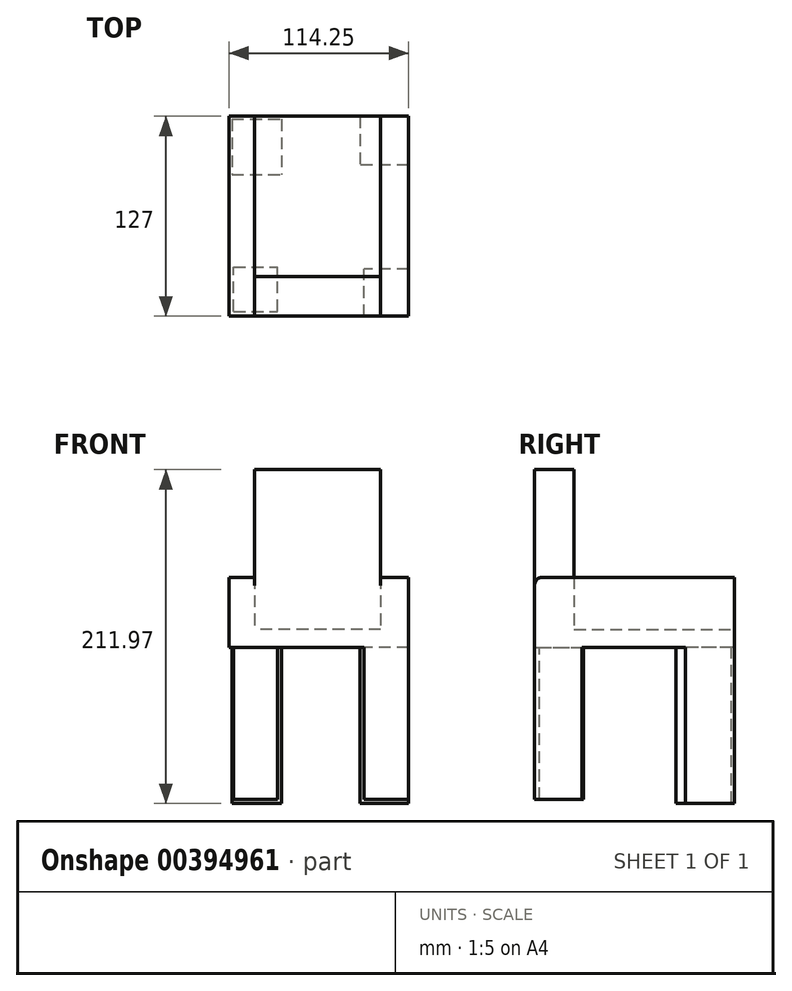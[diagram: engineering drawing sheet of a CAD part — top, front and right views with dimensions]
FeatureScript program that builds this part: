
annotation { "Feature Type Name" : "Feature", "Feature Type Description" : "" }
export const myFeature = defineFeature(function(context is Context, id is Id, definition is map)
    precondition{}
    {
        {
            var Q0;
            Q0=qCreatedBy(makeId("Front.planeOp"),FACE);
            var sketch = newSketch(context, id + "F0", { "sketchPlane" : qUnion([Q0])});
            skLineSegment(sketch, "E0.bottom", {"start": v(-64.3, 40.12) * mm, "end": v(49.96, 40.12) * mm});
            skLineSegment(sketch, "E0.top", {"start": v(-64.3, -37.67) * mm, "end": v(49.96, -37.67) * mm});
            skLineSegment(sketch, "E0.left", {"start": v(-64.3, 40.12) * mm, "end": v(-64.3, -37.67) * mm});
            skLineSegment(sketch, "E0.right", {"start": v(49.96, 40.12) * mm, "end": v(49.96, -37.67) * mm});
            skLineSegment(sketch, "E1.bottom", {"start": v(41.06, 40.12) * mm, "end": v(52.67, 40.12) * mm});
            skLineSegment(sketch, "E1.top", {"start": v(41.06, 40.12) * mm, "end": v(52.67, 40.12) * mm});
            skLineSegment(sketch, "E1.left", {"start": v(41.06, 40.12) * mm, "end": v(41.06, 40.12) * mm});
            skLineSegment(sketch, "E1.right", {"start": v(52.67, 40.12) * mm, "end": v(52.67, 40.12) * mm});
            skSolve(sketch);
        }
        {
            var Q0;
            {var subQ1=sQuery(id+"F0.wireOp",EDGE,"E0.bottom");Q0=makeQuery(id+"F0.imprint","IMPRINT",FACE,{"disambiguationData":[TD([[makeQuery(id+"F0.imprint","IMPRINT",EDGE,{"derivedFrom":subQ1}),-1.0]])]});}
            extrude(context, id + "F1", {"entities" : qUnion([Q0]), "oppositeDirection" : true, "depth" : 127 * mm});
        }
        {
            var Q0;
            Q0=makeQuery(id+"F1.opExtrude","CAP_FACE",FACE,{"disambiguationData":[OSD([sQuery(id+"F0.wireOp",EDGE,"E0.bottom"),sQuery(id+"F0.wireOp",EDGE,"E0.top"),sQuery(id+"F0.wireOp",EDGE,"E0.left"),sQuery(id+"F0.wireOp",EDGE,"E0.right"),sQuery(id+"F0.wireOp",EDGE,"E1.top")])],"isStart":false});
            var sketch = newSketch(context, id + "F2", { "sketchPlane" : qUnion([Q0])});
            skLineSegment(sketch, "E2.bottom", {"start": v(-32.22, 40.12) * mm, "end": v(48, 40.12) * mm});
            skLineSegment(sketch, "E2.top", {"start": v(-32.22, -26.36) * mm, "end": v(48, -26.36) * mm});
            skLineSegment(sketch, "E2.left", {"start": v(-32.22, 40.12) * mm, "end": v(-32.22, -26.36) * mm});
            skLineSegment(sketch, "E2.right", {"start": v(48, 40.12) * mm, "end": v(48, -26.36) * mm});
            skSolve(sketch);
        }
        {
            var Q0;
            Q0 = qSketchRegion(id + "F2", true);
            extrude(context, id + "F3", {"entities" : qUnion([Q0]), "operationType" : NewBodyOperationType.REMOVE, "oppositeDirection" : true, "depth" : 127 * mm});
        }
        {
            var Q0;
            Q0=makeQuery(id+"F1.opExtrude","CAP_FACE",FACE,{"disambiguationData":[OSD([sQuery(id+"F0.wireOp",EDGE,"E0.bottom"),sQuery(id+"F0.wireOp",EDGE,"E0.top"),sQuery(id+"F0.wireOp",EDGE,"E0.left"),sQuery(id+"F0.wireOp",EDGE,"E0.right"),sQuery(id+"F0.wireOp",EDGE,"E1.top")])],"isStart":false});
            var sketch = newSketch(context, id + "F4", { "sketchPlane" : qUnion([Q0])});
            skLineSegment(sketch, "E3.bottom", {"start": v(-49.96, 40.12) * mm, "end": v(-32.22, 40.12) * mm});
            skLineSegment(sketch, "E3.top", {"start": v(-49.96, 6.88) * mm, "end": v(-32.22, 6.88) * mm});
            skLineSegment(sketch, "E3.left", {"start": v(-49.96, 40.12) * mm, "end": v(-49.96, 6.88) * mm});
            skLineSegment(sketch, "E3.right", {"start": v(-32.22, 40.12) * mm, "end": v(-32.22, 6.88) * mm});
            skLineSegment(sketch, "E4.bottom", {"start": v(48, 40.12) * mm, "end": v(64.3, 40.12) * mm});
            skLineSegment(sketch, "E4.top", {"start": v(48, 6.88) * mm, "end": v(64.3, 6.88) * mm});
            skLineSegment(sketch, "E4.left", {"start": v(48, 40.12) * mm, "end": v(48, 6.88) * mm});
            skLineSegment(sketch, "E4.right", {"start": v(64.3, 40.12) * mm, "end": v(64.3, 6.88) * mm});
            skSolve(sketch);
        }
        {
            var Q0;
            Q0 = qSketchRegion(id + "F4", true);
            extrude(context, id + "F5", {"entities" : qUnion([Q0]), "operationType" : NewBodyOperationType.REMOVE, "oppositeDirection" : true, "depth" : 152.4 * mm});
        }
        {
            var Q0;
            Q0=makeQuery(id+"F3.boolean.opBoolean","COPY",FACE,{"derivedFrom":makeQuery(id+"F3.opExtrude","SWEPT_FACE",FACE,{"disambiguationData":[OSD([sQuery(id+"F2.wireOp",EDGE,"E2.top")])]})});
            var sketch = newSketch(context, id + "F6", { "sketchPlane" : qUnion([Q0])});
            skLineSegment(sketch, "E5.bottom", {"start": v(-48, 0) * mm, "end": v(32.22, 0) * mm});
            skLineSegment(sketch, "E5.top", {"start": v(-48, 25) * mm, "end": v(32.22, 25) * mm});
            skLineSegment(sketch, "E5.left", {"start": v(-48, 0) * mm, "end": v(-48, 25) * mm});
            skLineSegment(sketch, "E5.right", {"start": v(32.22, 0) * mm, "end": v(32.22, 25) * mm});
            skSolve(sketch);
        }
        {
            var Q0;
            Q0 = qSketchRegion(id + "F6", true);
            extrude(context, id + "F7", {"entities" : qUnion([Q0]), "operationType" : NewBodyOperationType.ADD, "depth" : 101.6 * mm});
        }
        {
            var Q0;
            Q0=makeQuery(id+"F1.opExtrude","SWEPT_FACE",FACE,{"disambiguationData":[OSD([sQuery(id+"F0.wireOp",EDGE,"E0.top")])]});
            var sketch = newSketch(context, id + "F8", { "sketchPlane" : qUnion([Q0])});
            skLineSegment(sketch, "E6.bottom", {"start": v(-61.28, -3.06) * mm, "end": v(-33.32, -3.06) * mm});
            skLineSegment(sketch, "E6.top", {"start": v(-61.28, -31.03) * mm, "end": v(-33.32, -31.03) * mm});
            skLineSegment(sketch, "E6.left", {"start": v(-61.28, -3.06) * mm, "end": v(-61.28, -31.03) * mm});
            skLineSegment(sketch, "E6.right", {"start": v(-33.32, -3.06) * mm, "end": v(-33.32, -31.03) * mm});
            skSolve(sketch);
        }
        {
            var Q0;
            Q0 = qSketchRegion(id + "F8", true);
            extrude(context, id + "F9", {"entities" : qUnion([Q0]), "operationType" : NewBodyOperationType.ADD, "depth" : 152.4 * mm});
        }
        {
            var Q0;
            Q0=makeQuery(id+"F9.opExtrude","CAP_FACE",FACE,{"disambiguationData":[OSD([sQuery(id+"F8.wireOp",EDGE,"E6.bottom"),sQuery(id+"F8.wireOp",EDGE,"E6.top"),sQuery(id+"F8.wireOp",EDGE,"E6.left"),sQuery(id+"F8.wireOp",EDGE,"E6.right")])],"isStart":false});
            extrude(context, id + "F10", {"entities" : qUnion([Q0]), "operationType" : NewBodyOperationType.ADD, "depth" : 50.8 * mm});
        }
        {
            var Q0;
            Q0=makeQuery(id+"F10.opExtrude","CAP_FACE",FACE,{"disambiguationData":[OSD([sQuery(id+"F8.wireOp",EDGE,"E6.bottom"),sQuery(id+"F8.wireOp",EDGE,"E6.top"),sQuery(id+"F8.wireOp",EDGE,"E6.left"),sQuery(id+"F8.wireOp",EDGE,"E6.right")])],"isStart":false});
            extrude(context, id + "F11", {"entities" : qUnion([Q0]), "operationType" : NewBodyOperationType.REMOVE, "oppositeDirection" : true, "depth" : 106.68 * mm});
        }
        {
            var Q0;
            Q0=makeQuery(id+"F1.opExtrude","SWEPT_FACE",FACE,{"disambiguationData":[OSD([sQuery(id+"F0.wireOp",EDGE,"E0.top")])]});
            var sketch = newSketch(context, id + "F12", { "sketchPlane" : qUnion([Q0])});
            skLineSegment(sketch, "E7.bottom", {"start": v(49.96, 0) * mm, "end": v(21.55, 0) * mm});
            skLineSegment(sketch, "E7.top", {"start": v(49.96, -30.02) * mm, "end": v(21.55, -30.02) * mm});
            skLineSegment(sketch, "E7.left", {"start": v(49.96, 0) * mm, "end": v(49.96, -30.02) * mm});
            skLineSegment(sketch, "E7.right", {"start": v(21.55, 0) * mm, "end": v(21.55, -30.02) * mm});
            skSolve(sketch);
        }
        {
            var Q0;
            Q0 = qSketchRegion(id + "F12", true);
            extrude(context, id + "F13", {"entities" : qUnion([Q0]), "operationType" : NewBodyOperationType.ADD, "depth" : 96.52 * mm});
        }
        {
            var Q0;
            Q0=makeQuery(id+"F1.opExtrude","SWEPT_FACE",FACE,{"disambiguationData":[OSD([sQuery(id+"F0.wireOp",EDGE,"E0.top")])]});
            var sketch = newSketch(context, id + "F14", { "sketchPlane" : qUnion([Q0])});
            skLineSegment(sketch, "E8.bottom", {"start": v(49.96, -127) * mm, "end": v(19.06, -127) * mm});
            skLineSegment(sketch, "E8.top", {"start": v(49.96, -95.81) * mm, "end": v(19.06, -95.81) * mm});
            skLineSegment(sketch, "E8.left", {"start": v(49.96, -127) * mm, "end": v(49.96, -95.81) * mm});
            skLineSegment(sketch, "E8.right", {"start": v(19.06, -127) * mm, "end": v(19.06, -95.81) * mm});
            skSolve(sketch);
        }
        {
            var Q0;
            Q0 = qSketchRegion(id + "F14", true);
            extrude(context, id + "F15", {"entities" : qUnion([Q0]), "operationType" : NewBodyOperationType.ADD, "depth" : 99.06 * mm});
        }
        {
            var Q0;
            Q0=makeQuery(id+"F1.opExtrude","SWEPT_FACE",FACE,{"disambiguationData":[OSD([sQuery(id+"F0.wireOp",EDGE,"E0.top")])]});
            var sketch = newSketch(context, id + "F16", { "sketchPlane" : qUnion([Q0])});
            skLineSegment(sketch, "E9.bottom", {"start": v(-62.34, -125.03) * mm, "end": v(-30.7, -125.03) * mm});
            skLineSegment(sketch, "E9.top", {"start": v(-62.34, -89.87) * mm, "end": v(-30.7, -89.87) * mm});
            skLineSegment(sketch, "E9.left", {"start": v(-62.34, -125.03) * mm, "end": v(-62.34, -89.87) * mm});
            skLineSegment(sketch, "E9.right", {"start": v(-30.7, -125.03) * mm, "end": v(-30.7, -89.87) * mm});
            skSolve(sketch);
        }
        {
            var Q0;
            Q0 = qSketchRegion(id + "F16", true);
            extrude(context, id + "F17", {"entities" : qUnion([Q0]), "operationType" : NewBodyOperationType.ADD, "depth" : 99.06 * mm});
        }
        {
            var Q0;
            Q0=makeQuery(id+"F5.boolean.opBoolean","INTERSECT",EDGE,{"derivedFrom":[makeQuery(id+"F1.opExtrude","CAP_FACE",FACE,{"disambiguationData":[OSD([sQuery(id+"F0.wireOp",EDGE,"E0.bottom"),sQuery(id+"F0.wireOp",EDGE,"E0.top"),sQuery(id+"F0.wireOp",EDGE,"E0.left"),sQuery(id+"F0.wireOp",EDGE,"E0.right"),sQuery(id+"F0.wireOp",EDGE,"E1.top")])],"isStart":true}),makeQuery(id+"F5.opExtrude","SWEPT_FACE",FACE,{"disambiguationData":[OSD([sQuery(id+"F4.wireOp",EDGE,"E4.top")])]})]});
            fillet(context, id + "F18", {"entities" : qUnion([Q0]), "radius" : 5.08 * mm, "tangentPropagation" : true, "allowEdgeOverflow" : false});
        }
        {
            var Q0;
            Q0=makeQuery(id+"F5.boolean.opBoolean","INTERSECT",EDGE,{"derivedFrom":[makeQuery(id+"F1.opExtrude","CAP_FACE",FACE,{"disambiguationData":[OSD([sQuery(id+"F0.wireOp",EDGE,"E0.bottom"),sQuery(id+"F0.wireOp",EDGE,"E0.top"),sQuery(id+"F0.wireOp",EDGE,"E0.left"),sQuery(id+"F0.wireOp",EDGE,"E0.right"),sQuery(id+"F0.wireOp",EDGE,"E1.top")])],"isStart":true}),makeQuery(id+"F5.opExtrude","SWEPT_FACE",FACE,{"disambiguationData":[OSD([sQuery(id+"F4.wireOp",EDGE,"E3.top")])]})]});
            fillet(context, id + "F19", {"entities" : qUnion([Q0]), "radius" : 5.08 * mm, "tangentPropagation" : true, "allowEdgeOverflow" : false});
        }
    });
